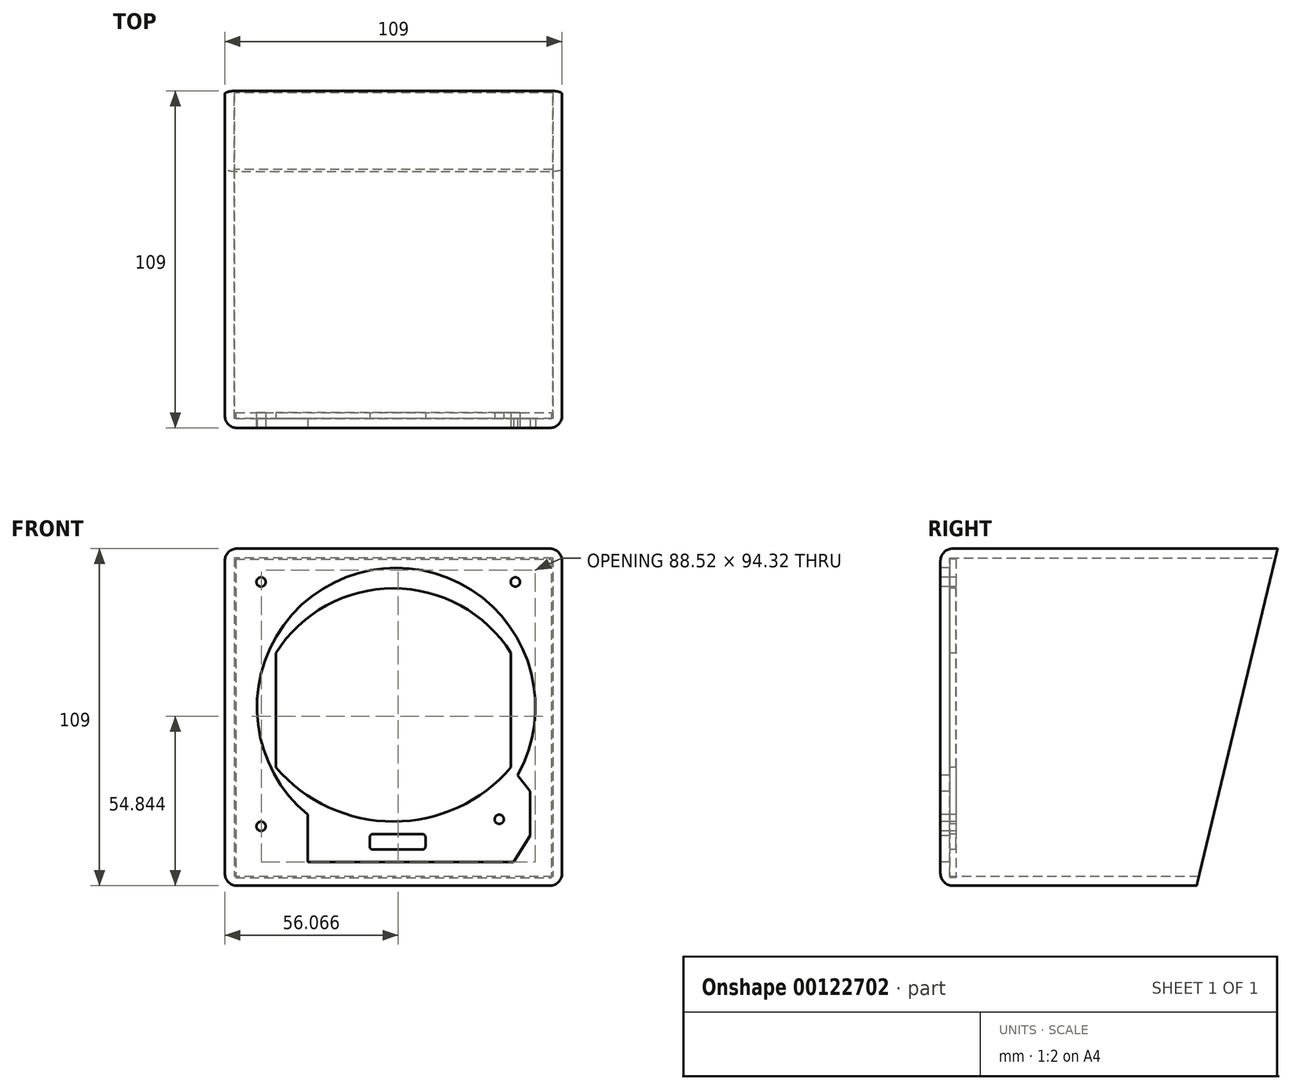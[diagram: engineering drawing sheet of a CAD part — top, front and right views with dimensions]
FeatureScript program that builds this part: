
annotation { "Feature Type Name" : "Feature", "Feature Type Description" : "" }
export const myFeature = defineFeature(function(context is Context, id is Id, definition is map)
    precondition{}
    {
        {
            var Q0;
            Q0=qCreatedBy(makeId("Right.planeOp"),FACE);
            var sketch = newSketch(context, id + "F0", { "sketchPlane" : qUnion([Q0])});
            skLineSegment(sketch, "E0", {"start": v(55.75, 41.61) * mm, "end": v(25.47, -84.48) * mm, "construction": true});
            skLineSegment(sketch, "E1", {"start": v(25.47, -84.48) * mm, "end": v(-51.21, -84.48) * mm, "construction": true});
            skLineSegment(sketch, "E2", {"start": v(58.95, 54.96) * mm, "end": v(32.78, -54.04) * mm});
            skLineSegment(sketch, "E3", {"start": v(32.78, -54.04) * mm, "end": v(-50.05, -54.04) * mm});
            skLineSegment(sketch, "E4", {"start": v(-50.05, -54.04) * mm, "end": v(-50.05, 54.96) * mm});
            skLineSegment(sketch, "E5", {"start": v(-50.05, 54.96) * mm, "end": v(58.95, 54.96) * mm});
            skSolve(sketch);
        }
        {
            var Q0;
            Q0=makeQuery(id+"F0.imprint","IMPRINT",FACE,{"disambiguationData":[TD([[makeQuery(id+"F0.imprint","IMPRINT",EDGE,{"derivedFrom":sQuery(id+"F0.wireOp",EDGE,"E2")}),-1.0]])]});
            extrude(context, id + "F1", {"entities" : qUnion([Q0]), "depth" : 109 * mm});
        }
        {
            var Q0;
            Q0=makeQuery(id+"F1.opExtrude","SWEPT_FACE",FACE,{"disambiguationData":[OSD([sQuery(id+"F0.wireOp",EDGE,"E2")])]});
            shell(context, id + "F2", {"entities" : qUnion([Q0]), "thickness" : 3 * mm});
        }
        {
            var Q0;
            Q0=makeQuery(id+"F1.opExtrude","SWEPT_FACE",FACE,{"disambiguationData":[OSD([sQuery(id+"F0.wireOp",EDGE,"E4")])]});
            var sketch = newSketch(context, id + "F3", { "sketchPlane" : qUnion([Q0])});
            skCircle(sketch, "E6", {"center": v(55.4, 3.74) * mm, "radius": 45 * mm});
            skLineSegment(sketch, "E7", {"start": v(0, 54.96) * mm, "end": v(0, -54.04) * mm, "construction": true});
            skLineSegment(sketch, "E8", {"start": v(0, -54.04) * mm, "end": v(109, -54.04) * mm, "construction": true});
            skLineSegment(sketch, "E9", {"start": v(109, -54.04) * mm, "end": v(109, 54.96) * mm, "construction": true});
            skLineSegment(sketch, "E10", {"start": v(109, 54.96) * mm, "end": v(0, 54.96) * mm, "construction": true});
            skLineSegment(sketch, "E11", {"start": v(26.84, -31.04) * mm, "end": v(26.84, -46.35) * mm});
            skLineSegment(sketch, "E12", {"start": v(26.84, -46.35) * mm, "end": v(93.38, -46.35) * mm});
            skLineSegment(sketch, "E13", {"start": v(93.38, -46.35) * mm, "end": v(98.74, -37.86) * mm});
            skLineSegment(sketch, "E14", {"start": v(98.74, -37.86) * mm, "end": v(98.74, -23.5) * mm});
            skLineSegment(sketch, "E15", {"start": v(98.74, -23.5) * mm, "end": v(94.63, -18.3) * mm});
            skSolve(sketch);
        }
        {
            var Q0;
            Q0=qSketchRegion(id+"F3",true);
            extrude(context, id + "F4", {"entities" : qUnion([Q0]), "operationType" : NewBodyOperationType.REMOVE, "oppositeDirection" : true, "depth" : 25 * mm});
        }
        {
            var Q0;
            Q0=qCreatedBy(makeId("Top.planeOp"),FACE);
            var sketch = newSketch(context, id + "F5", { "sketchPlane" : qUnion([Q0])});
            skLineSegment(sketch, "E16.bottom", {"start": v(3.5, -47.05) * mm, "end": v(105.5, -47.05) * mm});
            skLineSegment(sketch, "E16.top", {"start": v(3.5, -45.05) * mm, "end": v(105.5, -45.05) * mm});
            skLineSegment(sketch, "E16.left", {"start": v(3.5, -45.05) * mm, "end": v(3.5, -47.05) * mm});
            skLineSegment(sketch, "E16.right", {"start": v(105.5, -45.05) * mm, "end": v(105.5, -47.05) * mm});
            skSolve(sketch);
        }
        {
            var Q0;
            Q0=qSketchRegion(id+"F5",true);
            extrude(context, id + "F6", {"entities" : qUnion([Q0]), "depth" : 51.5 * mm, "hasSecondDirection" : true, "secondDirectionOppositeDirection" : true, "secondDirectionDepth" : 51.5 * mm});
        }
        {
            var Q0;
            {var subQ1=sQuery(id+"F3.wireOp",EDGE,"E11");Q0=makeQuery(id+"F3.imprint","IMPRINT",FACE,{"disambiguationData":[TD([[makeQuery(id+"F3.imprint","IMPRINT",EDGE,{"derivedFrom":subQ1}),-1.0]])]});}
            var sketch = newSketch(context, id + "F7", { "sketchPlane" : qUnion([Q0])});
            skLineSegment(sketch, "E17", {"start": v(16.5, 21.22) * mm, "end": v(16.5, -15.78) * mm});
            skLineSegment(sketch, "E18", {"start": v(92.5, 21.22) * mm, "end": v(92.5, -15.78) * mm});
            skArc(sketch, "E19", {"start": v(92.5, 21.22) * mm, "mid": v(54.5, 42.11) * mm, "end": v(16.5, 21.22) * mm});
            skArc(sketch, "E20", {"start": v(16.5, -15.78) * mm, "mid": v(54.5, -33.29) * mm, "end": v(92.5, -15.78) * mm});
            skLineSegment(sketch, "E21.bottom", {"start": v(47.85, -37.37) * mm, "end": v(63.85, -37.37) * mm});
            skLineSegment(sketch, "E21.top", {"start": v(47.85, -42.37) * mm, "end": v(63.85, -42.37) * mm});
            skLineSegment(sketch, "E21.left", {"start": v(46.85, -38.37) * mm, "end": v(46.85, -41.37) * mm});
            skLineSegment(sketch, "E21.right", {"start": v(64.85, -38.37) * mm, "end": v(64.85, -41.37) * mm});
            skPoint(sketch, "E22.visualSharp", {"position": v(46.85, -37.37) * mm});
            skArc(sketch, "E22.filletArc", {"start": v(47.85, -37.37) * mm, "mid": v(47.14, -37.66) * mm, "end": v(46.85, -38.37) * mm});
            skPoint(sketch, "E23.visualSharp", {"position": v(46.85, -42.37) * mm});
            skArc(sketch, "E23.filletArc", {"start": v(46.85, -41.37) * mm, "mid": v(47.14, -42.07) * mm, "end": v(47.85, -42.37) * mm});
            skPoint(sketch, "E24.visualSharp", {"position": v(64.85, -37.37) * mm});
            skArc(sketch, "E24.filletArc", {"start": v(64.85, -38.37) * mm, "mid": v(64.55, -37.66) * mm, "end": v(63.85, -37.37) * mm});
            skPoint(sketch, "E25.visualSharp", {"position": v(64.85, -42.37) * mm});
            skArc(sketch, "E25.filletArc", {"start": v(63.85, -42.37) * mm, "mid": v(64.55, -42.07) * mm, "end": v(64.85, -41.37) * mm});
            skCircle(sketch, "E26", {"center": v(88.68, -32.55) * mm, "radius": 1.5 * mm});
            skCircle(sketch, "E27", {"center": v(11.7, 44.17) * mm, "radius": 1.5 * mm});
            skCircle(sketch, "E28", {"center": v(11.7, -34.82) * mm, "radius": 1.5 * mm});
            skCircle(sketch, "E29", {"center": v(93.9, 44.17) * mm, "radius": 1.5 * mm});
            skSolve(sketch);
        }
        {
            var Q0;
            Q0=qSketchRegion(id+"F7",true);
            extrude(context, id + "F8", {"entities" : qUnion([Q0]), "operationType" : NewBodyOperationType.REMOVE, "oppositeDirection" : true, "depth" : 25 * mm});
        }
        {
            var Q0;
            Q0=makeQuery(id+"F1.opExtrude","CAP_EDGE",EDGE,{"disambiguationData":[OSD([sQuery(id+"F0.wireOp",EDGE,"E4")])],"isStart":true});
            var Q1;
            Q1=makeQuery(id+"F1.opExtrude","SWEPT_EDGE",EDGE,{"disambiguationData":[OSD([sQuery(id+"F0.wireOp",EDGE,"E4"),sQuery(id+"F0.wireOp",EDGE,"E5")])]});
            var Q2;
            Q2=makeQuery(id+"F1.opExtrude","CAP_EDGE",EDGE,{"disambiguationData":[OSD([sQuery(id+"F0.wireOp",EDGE,"E4")])],"isStart":false});
            var Q3;
            Q3=makeQuery(id+"F1.opExtrude","SWEPT_EDGE",EDGE,{"disambiguationData":[OSD([sQuery(id+"F0.wireOp",EDGE,"E3"),sQuery(id+"F0.wireOp",EDGE,"E4")])]});
            var Q4;
            Q4=makeQuery(id+"F1.opExtrude","CAP_EDGE",EDGE,{"disambiguationData":[OSD([sQuery(id+"F0.wireOp",EDGE,"E5")])],"isStart":true});
            var Q5;
            Q5=makeQuery(id+"F1.opExtrude","CAP_EDGE",EDGE,{"disambiguationData":[OSD([sQuery(id+"F0.wireOp",EDGE,"E3")])],"isStart":true});
            var Q6;
            Q6=makeQuery(id+"F1.opExtrude","CAP_EDGE",EDGE,{"disambiguationData":[OSD([sQuery(id+"F0.wireOp",EDGE,"E3")])],"isStart":false});
            var Q7;
            Q7=makeQuery(id+"F1.opExtrude","CAP_EDGE",EDGE,{"disambiguationData":[OSD([sQuery(id+"F0.wireOp",EDGE,"E5")])],"isStart":false});
            fillet(context, id + "F9", {"entities" : qUnion([Q0, Q1, Q2, Q3, Q4, Q5, Q6, Q7]), "radius" : 4 * mm, "tangentPropagation" : true, "allowEdgeOverflow" : false});
        }
    });
